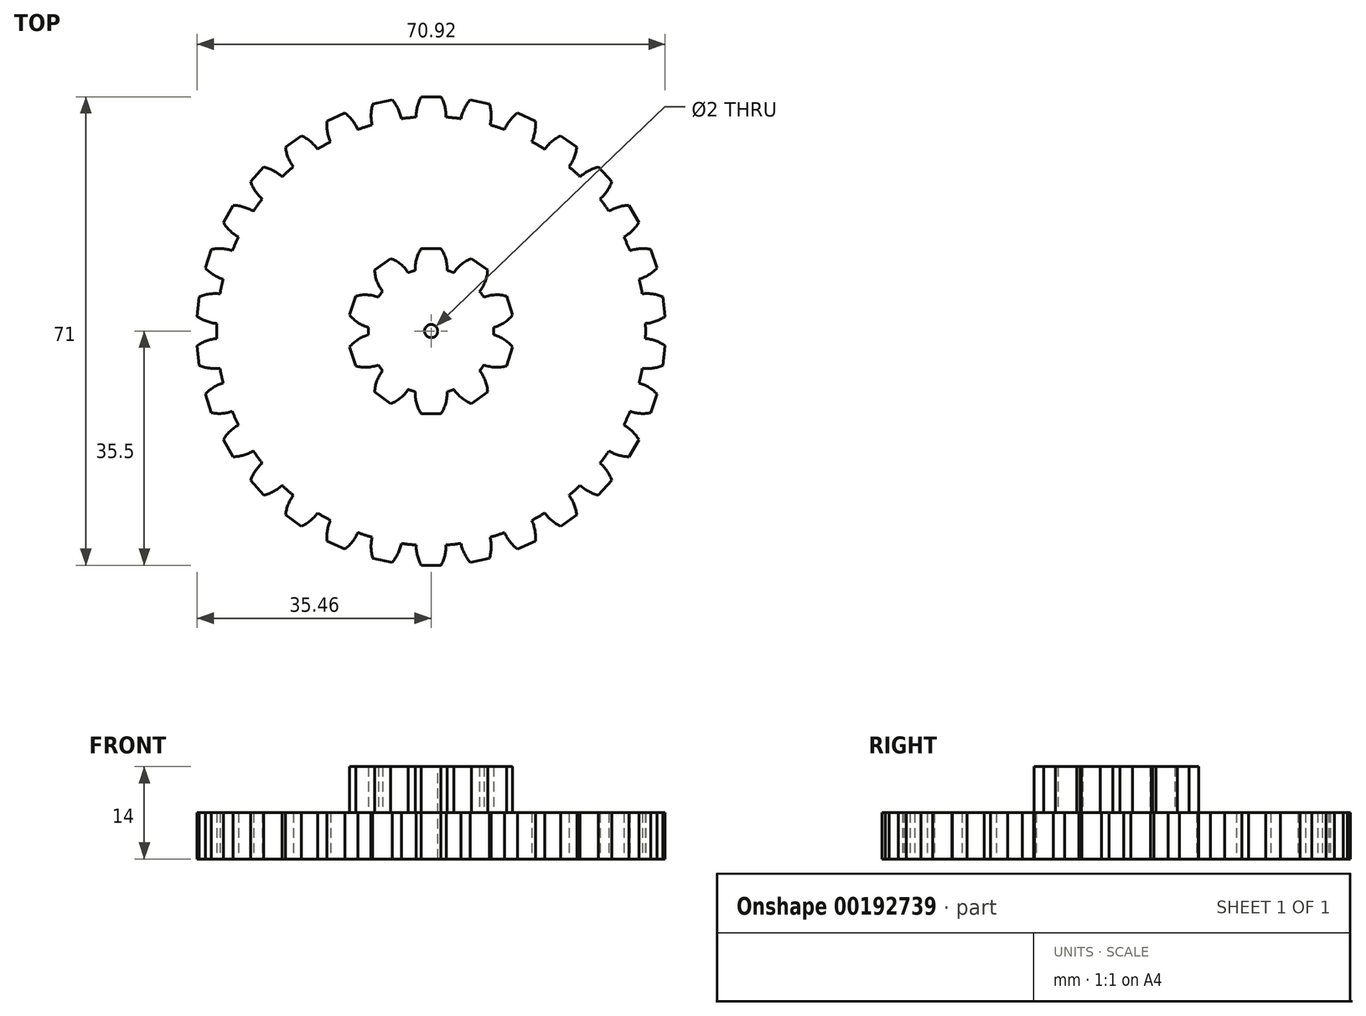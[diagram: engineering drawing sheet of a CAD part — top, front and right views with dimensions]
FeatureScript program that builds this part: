
annotation { "Feature Type Name" : "Feature", "Feature Type Description" : "" }
export const myFeature = defineFeature(function(context is Context, id is Id, definition is map)
    precondition{}
    {
        {
            var Q0;
            Q0=qCreatedBy(makeId("Top.planeOp"),FACE);
            var sketch = newSketch(context, id + "F0", { "sketchPlane" : qUnion([Q0])});
            skCircle(sketch, "E0", {"center": v(0, 0) * mm, "radius": 32.5 * mm});
            skLineSegment(sketch, "E1", {"start": v(0, 0) * mm, "end": v(0, 32.5) * mm, "construction": true});
            skLineSegment(sketch, "E2", {"start": v(0, 35.5) * mm, "end": v(-1.5, 35.5) * mm});
            skArc(sketch, "E3", {"start": v(-1.5, 35.5) * mm, "mid": v(-2.08, 34) * mm, "end": v(-2.26, 32.42) * mm});
            skLineSegment(sketch, "E4.MirrorCS", {"start": v(0, 35.5) * mm, "end": v(1.5, 35.5) * mm});
            skArc(sketch, "E5.MirrorCS", {"start": v(1.5, 35.5) * mm, "mid": v(2.08, 34) * mm, "end": v(2.26, 32.42) * mm});
            skArc(sketch, "E6.1.0", {"start": v(-8.85, 34.41) * mm, "mid": v(-9.1, 32.83) * mm, "end": v(-8.96, 31.24) * mm});
            skLineSegment(sketch, "E6.1.1", {"start": v(-7.38, 34.72) * mm, "end": v(-8.85, 34.41) * mm});
            skLineSegment(sketch, "E6.1.2", {"start": v(-7.38, 34.72) * mm, "end": v(-5.91, 35.04) * mm});
            skArc(sketch, "E6.1.3", {"start": v(-5.91, 35.04) * mm, "mid": v(-5.04, 33.7) * mm, "end": v(-4.53, 32.18) * mm});
            skArc(sketch, "E6.2.0", {"start": v(-15.8, 31.82) * mm, "mid": v(-15.73, 30.22) * mm, "end": v(-15.26, 28.7) * mm});
            skLineSegment(sketch, "E6.2.1", {"start": v(-14.44, 32.43) * mm, "end": v(-15.8, 31.82) * mm});
            skLineSegment(sketch, "E6.2.2", {"start": v(-14.44, 32.43) * mm, "end": v(-13.07, 33.04) * mm});
            skArc(sketch, "E6.2.3", {"start": v(-13.07, 33.04) * mm, "mid": v(-11.93, 31.92) * mm, "end": v(-11.12, 30.54) * mm});
            skArc(sketch, "E6.3.0", {"start": v(-22.08, 27.84) * mm, "mid": v(-21.67, 26.3) * mm, "end": v(-20.89, 24.9) * mm});
            skLineSegment(sketch, "E6.3.1", {"start": v(-20.87, 28.72) * mm, "end": v(-22.08, 27.84) * mm});
            skLineSegment(sketch, "E6.3.2", {"start": v(-20.87, 28.72) * mm, "end": v(-19.65, 29.6) * mm});
            skArc(sketch, "E6.3.3", {"start": v(-19.65, 29.6) * mm, "mid": v(-18.3, 28.74) * mm, "end": v(-17.22, 27.56) * mm});
            skArc(sketch, "E6.4.0", {"start": v(-27.39, 22.64) * mm, "mid": v(-26.67, 21.21) * mm, "end": v(-25.6, 20.01) * mm});
            skLineSegment(sketch, "E6.4.1", {"start": v(-26.38, 23.75) * mm, "end": v(-27.39, 22.64) * mm});
            skLineSegment(sketch, "E6.4.2", {"start": v(-26.38, 23.75) * mm, "end": v(-25.38, 24.87) * mm});
            skArc(sketch, "E6.4.3", {"start": v(-25.38, 24.87) * mm, "mid": v(-23.88, 24.3) * mm, "end": v(-22.58, 23.38) * mm});
            skArc(sketch, "E6.5.0", {"start": v(-31.5, 16.45) * mm, "mid": v(-30.5, 15.2) * mm, "end": v(-29.2, 14.25) * mm});
            skLineSegment(sketch, "E6.5.1", {"start": v(-30.74, 17.75) * mm, "end": v(-31.5, 16.45) * mm});
            skLineSegment(sketch, "E6.5.2", {"start": v(-30.74, 17.75) * mm, "end": v(-30, 19.05) * mm});
            skArc(sketch, "E6.5.3", {"start": v(-30, 19.05) * mm, "mid": v(-28.41, 18.8) * mm, "end": v(-26.95, 18.17) * mm});
            skArc(sketch, "E6.6.0", {"start": v(-34.23, 9.54) * mm, "mid": v(-32.99, 8.53) * mm, "end": v(-31.53, 7.86) * mm});
            skLineSegment(sketch, "E6.6.1", {"start": v(-33.76, 10.97) * mm, "end": v(-34.23, 9.54) * mm});
            skLineSegment(sketch, "E6.6.2", {"start": v(-33.76, 10.97) * mm, "end": v(-33.3, 12.4) * mm});
            skArc(sketch, "E6.6.3", {"start": v(-33.3, 12.4) * mm, "mid": v(-31.7, 12.49) * mm, "end": v(-30.13, 12.17) * mm});
            skArc(sketch, "E6.7.0", {"start": v(-35.46, 2.22) * mm, "mid": v(-34.04, 1.49) * mm, "end": v(-32.48, 1.14) * mm});
            skLineSegment(sketch, "E6.7.1", {"start": v(-35.3, 3.71) * mm, "end": v(-35.46, 2.22) * mm});
            skLineSegment(sketch, "E6.7.2", {"start": v(-35.3, 3.71) * mm, "end": v(-35.15, 5.2) * mm});
            skArc(sketch, "E6.7.3", {"start": v(-35.15, 5.2) * mm, "mid": v(-33.6, 5.62) * mm, "end": v(-32, 5.64) * mm});
            skArc(sketch, "E6.8.0", {"start": v(-35.15, -5.2) * mm, "mid": v(-33.6, -5.62) * mm, "end": v(-32, -5.64) * mm});
            skLineSegment(sketch, "E6.8.1", {"start": v(-35.3, -3.71) * mm, "end": v(-35.15, -5.2) * mm});
            skLineSegment(sketch, "E6.8.2", {"start": v(-35.3, -3.71) * mm, "end": v(-35.46, -2.22) * mm});
            skArc(sketch, "E6.8.3", {"start": v(-35.46, -2.22) * mm, "mid": v(-34.04, -1.49) * mm, "end": v(-32.48, -1.14) * mm});
            skArc(sketch, "E6.9.0", {"start": v(-33.3, -12.4) * mm, "mid": v(-31.7, -12.49) * mm, "end": v(-30.13, -12.17) * mm});
            skLineSegment(sketch, "E6.9.1", {"start": v(-33.76, -10.97) * mm, "end": v(-33.3, -12.4) * mm});
            skLineSegment(sketch, "E6.9.2", {"start": v(-33.76, -10.97) * mm, "end": v(-34.23, -9.54) * mm});
            skArc(sketch, "E6.9.3", {"start": v(-34.23, -9.54) * mm, "mid": v(-32.99, -8.53) * mm, "end": v(-31.53, -7.86) * mm});
            skArc(sketch, "E6.10.0", {"start": v(-30, -19.05) * mm, "mid": v(-28.41, -18.8) * mm, "end": v(-26.95, -18.17) * mm});
            skLineSegment(sketch, "E6.10.1", {"start": v(-30.74, -17.75) * mm, "end": v(-30, -19.05) * mm});
            skLineSegment(sketch, "E6.10.2", {"start": v(-30.74, -17.75) * mm, "end": v(-31.5, -16.45) * mm});
            skArc(sketch, "E6.10.3", {"start": v(-31.5, -16.45) * mm, "mid": v(-30.5, -15.2) * mm, "end": v(-29.2, -14.25) * mm});
            skArc(sketch, "E6.11.0", {"start": v(-25.38, -24.87) * mm, "mid": v(-23.88, -24.3) * mm, "end": v(-22.58, -23.38) * mm});
            skLineSegment(sketch, "E6.11.1", {"start": v(-26.38, -23.75) * mm, "end": v(-25.38, -24.87) * mm});
            skLineSegment(sketch, "E6.11.2", {"start": v(-26.38, -23.75) * mm, "end": v(-27.39, -22.64) * mm});
            skArc(sketch, "E6.11.3", {"start": v(-27.39, -22.64) * mm, "mid": v(-26.67, -21.21) * mm, "end": v(-25.6, -20.01) * mm});
            skArc(sketch, "E6.12.0", {"start": v(-19.65, -29.6) * mm, "mid": v(-18.3, -28.74) * mm, "end": v(-17.22, -27.56) * mm});
            skLineSegment(sketch, "E6.12.1", {"start": v(-20.87, -28.72) * mm, "end": v(-19.65, -29.6) * mm});
            skLineSegment(sketch, "E6.12.2", {"start": v(-20.87, -28.72) * mm, "end": v(-22.08, -27.84) * mm});
            skArc(sketch, "E6.12.3", {"start": v(-22.08, -27.84) * mm, "mid": v(-21.67, -26.3) * mm, "end": v(-20.89, -24.9) * mm});
            skArc(sketch, "E6.13.0", {"start": v(-13.07, -33.04) * mm, "mid": v(-11.93, -31.92) * mm, "end": v(-11.12, -30.54) * mm});
            skLineSegment(sketch, "E6.13.1", {"start": v(-14.44, -32.43) * mm, "end": v(-13.07, -33.04) * mm});
            skLineSegment(sketch, "E6.13.2", {"start": v(-14.44, -32.43) * mm, "end": v(-15.8, -31.82) * mm});
            skArc(sketch, "E6.13.3", {"start": v(-15.8, -31.82) * mm, "mid": v(-15.73, -30.22) * mm, "end": v(-15.26, -28.7) * mm});
            skArc(sketch, "E6.14.0", {"start": v(-5.91, -35.04) * mm, "mid": v(-5.04, -33.7) * mm, "end": v(-4.53, -32.18) * mm});
            skLineSegment(sketch, "E6.14.1", {"start": v(-7.38, -34.72) * mm, "end": v(-5.91, -35.04) * mm});
            skLineSegment(sketch, "E6.14.2", {"start": v(-7.38, -34.72) * mm, "end": v(-8.85, -34.41) * mm});
            skArc(sketch, "E6.14.3", {"start": v(-8.85, -34.41) * mm, "mid": v(-9.1, -32.83) * mm, "end": v(-8.96, -31.24) * mm});
            skArc(sketch, "E6.15.0", {"start": v(1.5, -35.5) * mm, "mid": v(2.08, -34) * mm, "end": v(2.26, -32.42) * mm});
            skLineSegment(sketch, "E6.15.1", {"start": v(0, -35.5) * mm, "end": v(1.5, -35.5) * mm});
            skLineSegment(sketch, "E6.15.2", {"start": v(0, -35.5) * mm, "end": v(-1.5, -35.5) * mm});
            skArc(sketch, "E6.15.3", {"start": v(-1.5, -35.5) * mm, "mid": v(-2.08, -34) * mm, "end": v(-2.26, -32.42) * mm});
            skArc(sketch, "E6.16.0", {"start": v(8.85, -34.41) * mm, "mid": v(9.1, -32.83) * mm, "end": v(8.96, -31.24) * mm});
            skLineSegment(sketch, "E6.16.1", {"start": v(7.38, -34.72) * mm, "end": v(8.85, -34.41) * mm});
            skLineSegment(sketch, "E6.16.2", {"start": v(7.38, -34.72) * mm, "end": v(5.91, -35.04) * mm});
            skArc(sketch, "E6.16.3", {"start": v(5.91, -35.04) * mm, "mid": v(5.04, -33.7) * mm, "end": v(4.53, -32.18) * mm});
            skArc(sketch, "E6.17.0", {"start": v(15.8, -31.82) * mm, "mid": v(15.73, -30.22) * mm, "end": v(15.26, -28.7) * mm});
            skLineSegment(sketch, "E6.17.1", {"start": v(14.44, -32.43) * mm, "end": v(15.8, -31.82) * mm});
            skLineSegment(sketch, "E6.17.2", {"start": v(14.44, -32.43) * mm, "end": v(13.07, -33.04) * mm});
            skArc(sketch, "E6.17.3", {"start": v(13.07, -33.04) * mm, "mid": v(11.93, -31.92) * mm, "end": v(11.12, -30.54) * mm});
            skArc(sketch, "E6.18.0", {"start": v(22.08, -27.84) * mm, "mid": v(21.67, -26.3) * mm, "end": v(20.89, -24.9) * mm});
            skLineSegment(sketch, "E6.18.1", {"start": v(20.87, -28.72) * mm, "end": v(22.08, -27.84) * mm});
            skLineSegment(sketch, "E6.18.2", {"start": v(20.87, -28.72) * mm, "end": v(19.65, -29.6) * mm});
            skArc(sketch, "E6.18.3", {"start": v(19.65, -29.6) * mm, "mid": v(18.3, -28.74) * mm, "end": v(17.22, -27.56) * mm});
            skArc(sketch, "E6.19.0", {"start": v(27.39, -22.64) * mm, "mid": v(26.67, -21.21) * mm, "end": v(25.6, -20.01) * mm});
            skLineSegment(sketch, "E6.19.1", {"start": v(26.38, -23.75) * mm, "end": v(27.39, -22.64) * mm});
            skLineSegment(sketch, "E6.19.2", {"start": v(26.38, -23.75) * mm, "end": v(25.38, -24.87) * mm});
            skArc(sketch, "E6.19.3", {"start": v(25.38, -24.87) * mm, "mid": v(23.88, -24.3) * mm, "end": v(22.58, -23.38) * mm});
            skArc(sketch, "E6.20.0", {"start": v(31.5, -16.45) * mm, "mid": v(30.5, -15.2) * mm, "end": v(29.2, -14.25) * mm});
            skLineSegment(sketch, "E6.20.1", {"start": v(30.74, -17.75) * mm, "end": v(31.5, -16.45) * mm});
            skLineSegment(sketch, "E6.20.2", {"start": v(30.74, -17.75) * mm, "end": v(30, -19.05) * mm});
            skArc(sketch, "E6.20.3", {"start": v(30, -19.05) * mm, "mid": v(28.41, -18.8) * mm, "end": v(26.95, -18.17) * mm});
            skArc(sketch, "E6.21.0", {"start": v(34.23, -9.54) * mm, "mid": v(32.99, -8.53) * mm, "end": v(31.53, -7.86) * mm});
            skLineSegment(sketch, "E6.21.1", {"start": v(33.76, -10.97) * mm, "end": v(34.23, -9.54) * mm});
            skLineSegment(sketch, "E6.21.2", {"start": v(33.76, -10.97) * mm, "end": v(33.3, -12.4) * mm});
            skArc(sketch, "E6.21.3", {"start": v(33.3, -12.4) * mm, "mid": v(31.7, -12.49) * mm, "end": v(30.13, -12.17) * mm});
            skArc(sketch, "E6.22.0", {"start": v(35.46, -2.22) * mm, "mid": v(34.04, -1.49) * mm, "end": v(32.48, -1.14) * mm});
            skLineSegment(sketch, "E6.22.1", {"start": v(35.3, -3.71) * mm, "end": v(35.46, -2.22) * mm});
            skLineSegment(sketch, "E6.22.2", {"start": v(35.3, -3.71) * mm, "end": v(35.15, -5.2) * mm});
            skArc(sketch, "E6.22.3", {"start": v(35.15, -5.2) * mm, "mid": v(33.6, -5.62) * mm, "end": v(32, -5.64) * mm});
            skArc(sketch, "E6.23.0", {"start": v(35.15, 5.2) * mm, "mid": v(33.6, 5.62) * mm, "end": v(32, 5.64) * mm});
            skLineSegment(sketch, "E6.23.1", {"start": v(35.3, 3.71) * mm, "end": v(35.15, 5.2) * mm});
            skLineSegment(sketch, "E6.23.2", {"start": v(35.3, 3.71) * mm, "end": v(35.46, 2.22) * mm});
            skArc(sketch, "E6.23.3", {"start": v(35.46, 2.22) * mm, "mid": v(34.04, 1.49) * mm, "end": v(32.48, 1.14) * mm});
            skArc(sketch, "E6.24.0", {"start": v(33.3, 12.4) * mm, "mid": v(31.7, 12.49) * mm, "end": v(30.13, 12.17) * mm});
            skLineSegment(sketch, "E6.24.1", {"start": v(33.76, 10.97) * mm, "end": v(33.3, 12.4) * mm});
            skLineSegment(sketch, "E6.24.2", {"start": v(33.76, 10.97) * mm, "end": v(34.23, 9.54) * mm});
            skArc(sketch, "E6.24.3", {"start": v(34.23, 9.54) * mm, "mid": v(32.99, 8.53) * mm, "end": v(31.53, 7.86) * mm});
            skArc(sketch, "E6.25.0", {"start": v(30, 19.05) * mm, "mid": v(28.41, 18.8) * mm, "end": v(26.95, 18.17) * mm});
            skLineSegment(sketch, "E6.25.1", {"start": v(30.74, 17.75) * mm, "end": v(30, 19.05) * mm});
            skLineSegment(sketch, "E6.25.2", {"start": v(30.74, 17.75) * mm, "end": v(31.5, 16.45) * mm});
            skArc(sketch, "E6.25.3", {"start": v(31.5, 16.45) * mm, "mid": v(30.5, 15.2) * mm, "end": v(29.2, 14.25) * mm});
            skArc(sketch, "E6.26.0", {"start": v(25.38, 24.87) * mm, "mid": v(23.88, 24.3) * mm, "end": v(22.58, 23.38) * mm});
            skLineSegment(sketch, "E6.26.1", {"start": v(26.38, 23.75) * mm, "end": v(25.38, 24.87) * mm});
            skLineSegment(sketch, "E6.26.2", {"start": v(26.38, 23.75) * mm, "end": v(27.39, 22.64) * mm});
            skArc(sketch, "E6.26.3", {"start": v(27.39, 22.64) * mm, "mid": v(26.67, 21.21) * mm, "end": v(25.6, 20.01) * mm});
            skArc(sketch, "E6.27.0", {"start": v(19.65, 29.6) * mm, "mid": v(18.3, 28.74) * mm, "end": v(17.22, 27.56) * mm});
            skLineSegment(sketch, "E6.27.1", {"start": v(20.87, 28.72) * mm, "end": v(19.65, 29.6) * mm});
            skLineSegment(sketch, "E6.27.2", {"start": v(20.87, 28.72) * mm, "end": v(22.08, 27.84) * mm});
            skArc(sketch, "E6.27.3", {"start": v(22.08, 27.84) * mm, "mid": v(21.67, 26.3) * mm, "end": v(20.89, 24.9) * mm});
            skArc(sketch, "E6.28.0", {"start": v(13.07, 33.04) * mm, "mid": v(11.93, 31.92) * mm, "end": v(11.12, 30.54) * mm});
            skLineSegment(sketch, "E6.28.1", {"start": v(14.44, 32.43) * mm, "end": v(13.07, 33.04) * mm});
            skLineSegment(sketch, "E6.28.2", {"start": v(14.44, 32.43) * mm, "end": v(15.8, 31.82) * mm});
            skArc(sketch, "E6.28.3", {"start": v(15.8, 31.82) * mm, "mid": v(15.73, 30.22) * mm, "end": v(15.26, 28.7) * mm});
            skArc(sketch, "E6.29.0", {"start": v(5.91, 35.04) * mm, "mid": v(5.04, 33.7) * mm, "end": v(4.53, 32.18) * mm});
            skLineSegment(sketch, "E6.29.1", {"start": v(7.38, 34.72) * mm, "end": v(5.91, 35.04) * mm});
            skLineSegment(sketch, "E6.29.2", {"start": v(7.38, 34.72) * mm, "end": v(8.85, 34.41) * mm});
            skArc(sketch, "E6.29.3", {"start": v(8.85, 34.41) * mm, "mid": v(9.1, 32.83) * mm, "end": v(8.96, 31.24) * mm});
            skSolve(sketch);
        }
        {
            var Q0;
            Q0 = qSketchRegion(id + "F0", true);
            extrude(context, id + "F1", {"entities" : qUnion([Q0]), "depth" : 7 * mm});
        }
        {
            var Q0;
            Q0=makeQuery(id+"F1.opExtrude","CAP_FACE",FACE,{"disambiguationData":[OSD([sQuery(id+"F0.wireOp",EDGE,"E0"),sQuery(id+"F0.wireOp",EDGE,"E2"),sQuery(id+"F0.wireOp",EDGE,"E3"),sQuery(id+"F0.wireOp",EDGE,"E4.MirrorCS"),sQuery(id+"F0.wireOp",EDGE,"E5.MirrorCS"),sQuery(id+"F0.wireOp",EDGE,"E6.1.0"),sQuery(id+"F0.wireOp",EDGE,"E6.1.1"),sQuery(id+"F0.wireOp",EDGE,"E6.1.2"),sQuery(id+"F0.wireOp",EDGE,"E6.1.3"),sQuery(id+"F0.wireOp",EDGE,"E6.2.0"),sQuery(id+"F0.wireOp",EDGE,"E6.2.1"),sQuery(id+"F0.wireOp",EDGE,"E6.2.2"),sQuery(id+"F0.wireOp",EDGE,"E6.2.3"),sQuery(id+"F0.wireOp",EDGE,"E6.3.0"),sQuery(id+"F0.wireOp",EDGE,"E6.3.1"),sQuery(id+"F0.wireOp",EDGE,"E6.3.2"),sQuery(id+"F0.wireOp",EDGE,"E6.3.3"),sQuery(id+"F0.wireOp",EDGE,"E6.4.0"),sQuery(id+"F0.wireOp",EDGE,"E6.4.1"),sQuery(id+"F0.wireOp",EDGE,"E6.4.2"),sQuery(id+"F0.wireOp",EDGE,"E6.4.3"),sQuery(id+"F0.wireOp",EDGE,"E6.5.0"),sQuery(id+"F0.wireOp",EDGE,"E6.5.1"),sQuery(id+"F0.wireOp",EDGE,"E6.5.2"),sQuery(id+"F0.wireOp",EDGE,"E6.5.3"),sQuery(id+"F0.wireOp",EDGE,"E6.6.0"),sQuery(id+"F0.wireOp",EDGE,"E6.6.1"),sQuery(id+"F0.wireOp",EDGE,"E6.6.2"),sQuery(id+"F0.wireOp",EDGE,"E6.6.3"),sQuery(id+"F0.wireOp",EDGE,"E6.7.0"),sQuery(id+"F0.wireOp",EDGE,"E6.7.1"),sQuery(id+"F0.wireOp",EDGE,"E6.7.2"),sQuery(id+"F0.wireOp",EDGE,"E6.7.3"),sQuery(id+"F0.wireOp",EDGE,"E6.8.0"),sQuery(id+"F0.wireOp",EDGE,"E6.8.1"),sQuery(id+"F0.wireOp",EDGE,"E6.8.2"),sQuery(id+"F0.wireOp",EDGE,"E6.8.3"),sQuery(id+"F0.wireOp",EDGE,"E6.9.0"),sQuery(id+"F0.wireOp",EDGE,"E6.9.1"),sQuery(id+"F0.wireOp",EDGE,"E6.9.2"),sQuery(id+"F0.wireOp",EDGE,"E6.9.3"),sQuery(id+"F0.wireOp",EDGE,"E6.10.0"),sQuery(id+"F0.wireOp",EDGE,"E6.10.1"),sQuery(id+"F0.wireOp",EDGE,"E6.10.2"),sQuery(id+"F0.wireOp",EDGE,"E6.10.3"),sQuery(id+"F0.wireOp",EDGE,"E6.11.0"),sQuery(id+"F0.wireOp",EDGE,"E6.11.1"),sQuery(id+"F0.wireOp",EDGE,"E6.11.2"),sQuery(id+"F0.wireOp",EDGE,"E6.11.3"),sQuery(id+"F0.wireOp",EDGE,"E6.12.0"),sQuery(id+"F0.wireOp",EDGE,"E6.12.1"),sQuery(id+"F0.wireOp",EDGE,"E6.12.2"),sQuery(id+"F0.wireOp",EDGE,"E6.12.3"),sQuery(id+"F0.wireOp",EDGE,"E6.13.0"),sQuery(id+"F0.wireOp",EDGE,"E6.13.1"),sQuery(id+"F0.wireOp",EDGE,"E6.13.2"),sQuery(id+"F0.wireOp",EDGE,"E6.13.3"),sQuery(id+"F0.wireOp",EDGE,"E6.14.0"),sQuery(id+"F0.wireOp",EDGE,"E6.14.1"),sQuery(id+"F0.wireOp",EDGE,"E6.14.2"),sQuery(id+"F0.wireOp",EDGE,"E6.14.3"),sQuery(id+"F0.wireOp",EDGE,"E6.15.0"),sQuery(id+"F0.wireOp",EDGE,"E6.15.1"),sQuery(id+"F0.wireOp",EDGE,"E6.15.2"),sQuery(id+"F0.wireOp",EDGE,"E6.15.3"),sQuery(id+"F0.wireOp",EDGE,"E6.16.0"),sQuery(id+"F0.wireOp",EDGE,"E6.16.1"),sQuery(id+"F0.wireOp",EDGE,"E6.16.2"),sQuery(id+"F0.wireOp",EDGE,"E6.16.3"),sQuery(id+"F0.wireOp",EDGE,"E6.17.0"),sQuery(id+"F0.wireOp",EDGE,"E6.17.1"),sQuery(id+"F0.wireOp",EDGE,"E6.17.2"),sQuery(id+"F0.wireOp",EDGE,"E6.17.3"),sQuery(id+"F0.wireOp",EDGE,"E6.18.0"),sQuery(id+"F0.wireOp",EDGE,"E6.18.1"),sQuery(id+"F0.wireOp",EDGE,"E6.18.2"),sQuery(id+"F0.wireOp",EDGE,"E6.18.3"),sQuery(id+"F0.wireOp",EDGE,"E6.19.0"),sQuery(id+"F0.wireOp",EDGE,"E6.19.1"),sQuery(id+"F0.wireOp",EDGE,"E6.19.2"),sQuery(id+"F0.wireOp",EDGE,"E6.19.3"),sQuery(id+"F0.wireOp",EDGE,"E6.20.0"),sQuery(id+"F0.wireOp",EDGE,"E6.20.1"),sQuery(id+"F0.wireOp",EDGE,"E6.20.2"),sQuery(id+"F0.wireOp",EDGE,"E6.20.3"),sQuery(id+"F0.wireOp",EDGE,"E6.21.0"),sQuery(id+"F0.wireOp",EDGE,"E6.21.1"),sQuery(id+"F0.wireOp",EDGE,"E6.21.2"),sQuery(id+"F0.wireOp",EDGE,"E6.21.3"),sQuery(id+"F0.wireOp",EDGE,"E6.22.0"),sQuery(id+"F0.wireOp",EDGE,"E6.22.1"),sQuery(id+"F0.wireOp",EDGE,"E6.22.2"),sQuery(id+"F0.wireOp",EDGE,"E6.22.3"),sQuery(id+"F0.wireOp",EDGE,"E6.23.0"),sQuery(id+"F0.wireOp",EDGE,"E6.23.1"),sQuery(id+"F0.wireOp",EDGE,"E6.23.2"),sQuery(id+"F0.wireOp",EDGE,"E6.23.3"),sQuery(id+"F0.wireOp",EDGE,"E6.24.0"),sQuery(id+"F0.wireOp",EDGE,"E6.24.1"),sQuery(id+"F0.wireOp",EDGE,"E6.24.2"),sQuery(id+"F0.wireOp",EDGE,"E6.24.3"),sQuery(id+"F0.wireOp",EDGE,"E6.25.0"),sQuery(id+"F0.wireOp",EDGE,"E6.25.1"),sQuery(id+"F0.wireOp",EDGE,"E6.25.2"),sQuery(id+"F0.wireOp",EDGE,"E6.25.3"),sQuery(id+"F0.wireOp",EDGE,"E6.26.0"),sQuery(id+"F0.wireOp",EDGE,"E6.26.1"),sQuery(id+"F0.wireOp",EDGE,"E6.26.2"),sQuery(id+"F0.wireOp",EDGE,"E6.26.3"),sQuery(id+"F0.wireOp",EDGE,"E6.27.0"),sQuery(id+"F0.wireOp",EDGE,"E6.27.1"),sQuery(id+"F0.wireOp",EDGE,"E6.27.2"),sQuery(id+"F0.wireOp",EDGE,"E6.27.3"),sQuery(id+"F0.wireOp",EDGE,"E6.28.0"),sQuery(id+"F0.wireOp",EDGE,"E6.28.1"),sQuery(id+"F0.wireOp",EDGE,"E6.28.2"),sQuery(id+"F0.wireOp",EDGE,"E6.28.3"),sQuery(id+"F0.wireOp",EDGE,"E6.29.0"),sQuery(id+"F0.wireOp",EDGE,"E6.29.1"),sQuery(id+"F0.wireOp",EDGE,"E6.29.2"),sQuery(id+"F0.wireOp",EDGE,"E6.29.3")])],"isStart":false});
            var sketch = newSketch(context, id + "F2", { "sketchPlane" : qUnion([Q0])});
            skCircle(sketch, "E7", {"center": v(0, 0) * mm, "radius": 9.5 * mm});
            skLineSegment(sketch, "E8", {"start": v(0, 0) * mm, "end": v(0, 9.5) * mm, "construction": true});
            skLineSegment(sketch, "E9", {"start": v(0, 12.5) * mm, "end": v(-1.5, 12.5) * mm});
            skArc(sketch, "E10", {"start": v(-1.5, 12.5) * mm, "mid": v(-2.22, 10.92) * mm, "end": v(-2.4, 9.2) * mm});
            skLineSegment(sketch, "E11.MirrorCS", {"start": v(0, 12.5) * mm, "end": v(1.5, 12.5) * mm});
            skArc(sketch, "E12.MirrorCS", {"start": v(1.5, 12.5) * mm, "mid": v(2.22, 10.92) * mm, "end": v(2.4, 9.2) * mm});
            skArc(sketch, "E13.1.0", {"start": v(-8.56, 9.23) * mm, "mid": v(-8.21, 7.53) * mm, "end": v(-7.34, 6.03) * mm});
            skLineSegment(sketch, "E13.1.1", {"start": v(-7.35, 10.11) * mm, "end": v(-8.56, 9.23) * mm});
            skLineSegment(sketch, "E13.1.2", {"start": v(-7.35, 10.11) * mm, "end": v(-6.13, 11) * mm});
            skArc(sketch, "E13.1.3", {"start": v(-6.13, 11) * mm, "mid": v(-4.62, 10.14) * mm, "end": v(-3.46, 8.85) * mm});
            skArc(sketch, "E13.2.0", {"start": v(-12.35, 2.44) * mm, "mid": v(-11.07, 1.26) * mm, "end": v(-9.48, 0.56) * mm});
            skLineSegment(sketch, "E13.2.1", {"start": v(-11.89, 3.86) * mm, "end": v(-12.35, 2.44) * mm});
            skLineSegment(sketch, "E13.2.2", {"start": v(-11.89, 3.86) * mm, "end": v(-11.42, 5.29) * mm});
            skArc(sketch, "E13.2.3", {"start": v(-11.42, 5.29) * mm, "mid": v(-9.7, 5.48) * mm, "end": v(-8, 5.12) * mm});
            skArc(sketch, "E13.3.0", {"start": v(-11.42, -5.29) * mm, "mid": v(-9.7, -5.48) * mm, "end": v(-8, -5.12) * mm});
            skLineSegment(sketch, "E13.3.1", {"start": v(-11.89, -3.86) * mm, "end": v(-11.42, -5.29) * mm});
            skLineSegment(sketch, "E13.3.2", {"start": v(-11.89, -3.86) * mm, "end": v(-12.35, -2.44) * mm});
            skArc(sketch, "E13.3.3", {"start": v(-12.35, -2.44) * mm, "mid": v(-11.07, -1.26) * mm, "end": v(-9.48, -0.56) * mm});
            skArc(sketch, "E13.4.0", {"start": v(-6.13, -11) * mm, "mid": v(-4.62, -10.14) * mm, "end": v(-3.46, -8.85) * mm});
            skLineSegment(sketch, "E13.4.1", {"start": v(-7.35, -10.11) * mm, "end": v(-6.13, -11) * mm});
            skLineSegment(sketch, "E13.4.2", {"start": v(-7.35, -10.11) * mm, "end": v(-8.56, -9.23) * mm});
            skArc(sketch, "E13.4.3", {"start": v(-8.56, -9.23) * mm, "mid": v(-8.21, -7.53) * mm, "end": v(-7.34, -6.03) * mm});
            skArc(sketch, "E13.5.0", {"start": v(1.5, -12.5) * mm, "mid": v(2.22, -10.92) * mm, "end": v(2.4, -9.2) * mm});
            skLineSegment(sketch, "E13.5.1", {"start": v(0, -12.5) * mm, "end": v(1.5, -12.5) * mm});
            skLineSegment(sketch, "E13.5.2", {"start": v(0, -12.5) * mm, "end": v(-1.5, -12.5) * mm});
            skArc(sketch, "E13.5.3", {"start": v(-1.5, -12.5) * mm, "mid": v(-2.22, -10.92) * mm, "end": v(-2.4, -9.2) * mm});
            skArc(sketch, "E13.6.0", {"start": v(8.56, -9.23) * mm, "mid": v(8.21, -7.53) * mm, "end": v(7.34, -6.03) * mm});
            skLineSegment(sketch, "E13.6.1", {"start": v(7.35, -10.11) * mm, "end": v(8.56, -9.23) * mm});
            skLineSegment(sketch, "E13.6.2", {"start": v(7.35, -10.11) * mm, "end": v(6.13, -11) * mm});
            skArc(sketch, "E13.6.3", {"start": v(6.13, -11) * mm, "mid": v(4.62, -10.14) * mm, "end": v(3.46, -8.85) * mm});
            skArc(sketch, "E13.7.0", {"start": v(12.35, -2.44) * mm, "mid": v(11.07, -1.26) * mm, "end": v(9.48, -0.56) * mm});
            skLineSegment(sketch, "E13.7.1", {"start": v(11.89, -3.86) * mm, "end": v(12.35, -2.44) * mm});
            skLineSegment(sketch, "E13.7.2", {"start": v(11.89, -3.86) * mm, "end": v(11.42, -5.29) * mm});
            skArc(sketch, "E13.7.3", {"start": v(11.42, -5.29) * mm, "mid": v(9.7, -5.48) * mm, "end": v(8, -5.12) * mm});
            skArc(sketch, "E13.8.0", {"start": v(11.42, 5.29) * mm, "mid": v(9.7, 5.48) * mm, "end": v(8, 5.12) * mm});
            skLineSegment(sketch, "E13.8.1", {"start": v(11.89, 3.86) * mm, "end": v(11.42, 5.29) * mm});
            skLineSegment(sketch, "E13.8.2", {"start": v(11.89, 3.86) * mm, "end": v(12.35, 2.44) * mm});
            skArc(sketch, "E13.8.3", {"start": v(12.35, 2.44) * mm, "mid": v(11.07, 1.26) * mm, "end": v(9.48, 0.56) * mm});
            skArc(sketch, "E13.9.0", {"start": v(6.13, 11) * mm, "mid": v(4.62, 10.14) * mm, "end": v(3.46, 8.85) * mm});
            skLineSegment(sketch, "E13.9.1", {"start": v(7.35, 10.11) * mm, "end": v(6.13, 11) * mm});
            skLineSegment(sketch, "E13.9.2", {"start": v(7.35, 10.11) * mm, "end": v(8.56, 9.23) * mm});
            skArc(sketch, "E13.9.3", {"start": v(8.56, 9.23) * mm, "mid": v(8.21, 7.53) * mm, "end": v(7.34, 6.03) * mm});
            skSolve(sketch);
        }
        {
            var Q0;
            Q0 = qSketchRegion(id + "F2", true);
            extrude(context, id + "F3", {"entities" : qUnion([Q0]), "operationType" : NewBodyOperationType.ADD, "depth" : 7 * mm});
        }
        {
            var Q0;
            Q0=makeQuery(id+"F3.opExtrude","CAP_FACE",FACE,{"disambiguationData":[OSD([sQuery(id+"F2.wireOp",EDGE,"E7"),sQuery(id+"F2.wireOp",EDGE,"E9"),sQuery(id+"F2.wireOp",EDGE,"E10"),sQuery(id+"F2.wireOp",EDGE,"E11.MirrorCS"),sQuery(id+"F2.wireOp",EDGE,"E12.MirrorCS"),sQuery(id+"F2.wireOp",EDGE,"E13.1.0"),sQuery(id+"F2.wireOp",EDGE,"E13.1.1"),sQuery(id+"F2.wireOp",EDGE,"E13.1.2"),sQuery(id+"F2.wireOp",EDGE,"E13.1.3"),sQuery(id+"F2.wireOp",EDGE,"E13.2.0"),sQuery(id+"F2.wireOp",EDGE,"E13.2.1"),sQuery(id+"F2.wireOp",EDGE,"E13.2.2"),sQuery(id+"F2.wireOp",EDGE,"E13.2.3"),sQuery(id+"F2.wireOp",EDGE,"E13.3.0"),sQuery(id+"F2.wireOp",EDGE,"E13.3.1"),sQuery(id+"F2.wireOp",EDGE,"E13.3.2"),sQuery(id+"F2.wireOp",EDGE,"E13.3.3"),sQuery(id+"F2.wireOp",EDGE,"E13.4.0"),sQuery(id+"F2.wireOp",EDGE,"E13.4.1"),sQuery(id+"F2.wireOp",EDGE,"E13.4.2"),sQuery(id+"F2.wireOp",EDGE,"E13.4.3"),sQuery(id+"F2.wireOp",EDGE,"E13.5.0"),sQuery(id+"F2.wireOp",EDGE,"E13.5.1"),sQuery(id+"F2.wireOp",EDGE,"E13.5.2"),sQuery(id+"F2.wireOp",EDGE,"E13.5.3"),sQuery(id+"F2.wireOp",EDGE,"E13.6.0"),sQuery(id+"F2.wireOp",EDGE,"E13.6.1"),sQuery(id+"F2.wireOp",EDGE,"E13.6.2"),sQuery(id+"F2.wireOp",EDGE,"E13.6.3"),sQuery(id+"F2.wireOp",EDGE,"E13.7.0"),sQuery(id+"F2.wireOp",EDGE,"E13.7.1"),sQuery(id+"F2.wireOp",EDGE,"E13.7.2"),sQuery(id+"F2.wireOp",EDGE,"E13.7.3"),sQuery(id+"F2.wireOp",EDGE,"E13.8.0"),sQuery(id+"F2.wireOp",EDGE,"E13.8.1"),sQuery(id+"F2.wireOp",EDGE,"E13.8.2"),sQuery(id+"F2.wireOp",EDGE,"E13.8.3"),sQuery(id+"F2.wireOp",EDGE,"E13.9.0"),sQuery(id+"F2.wireOp",EDGE,"E13.9.1"),sQuery(id+"F2.wireOp",EDGE,"E13.9.2"),sQuery(id+"F2.wireOp",EDGE,"E13.9.3")])],"isStart":false});
            var sketch = newSketch(context, id + "F4", { "sketchPlane" : qUnion([Q0])});
            skCircle(sketch, "E14", {"center": v(0, 0) * mm, "radius": 1 * mm});
            skSolve(sketch);
        }
        {
            var Q0;
            Q0 = qSketchRegion(id + "F4", true);
            extrude(context, id + "F5", {"entities" : qUnion([Q0]), "operationType" : NewBodyOperationType.REMOVE, "oppositeDirection" : true, "depth" : 25 * mm});
        }
    });
